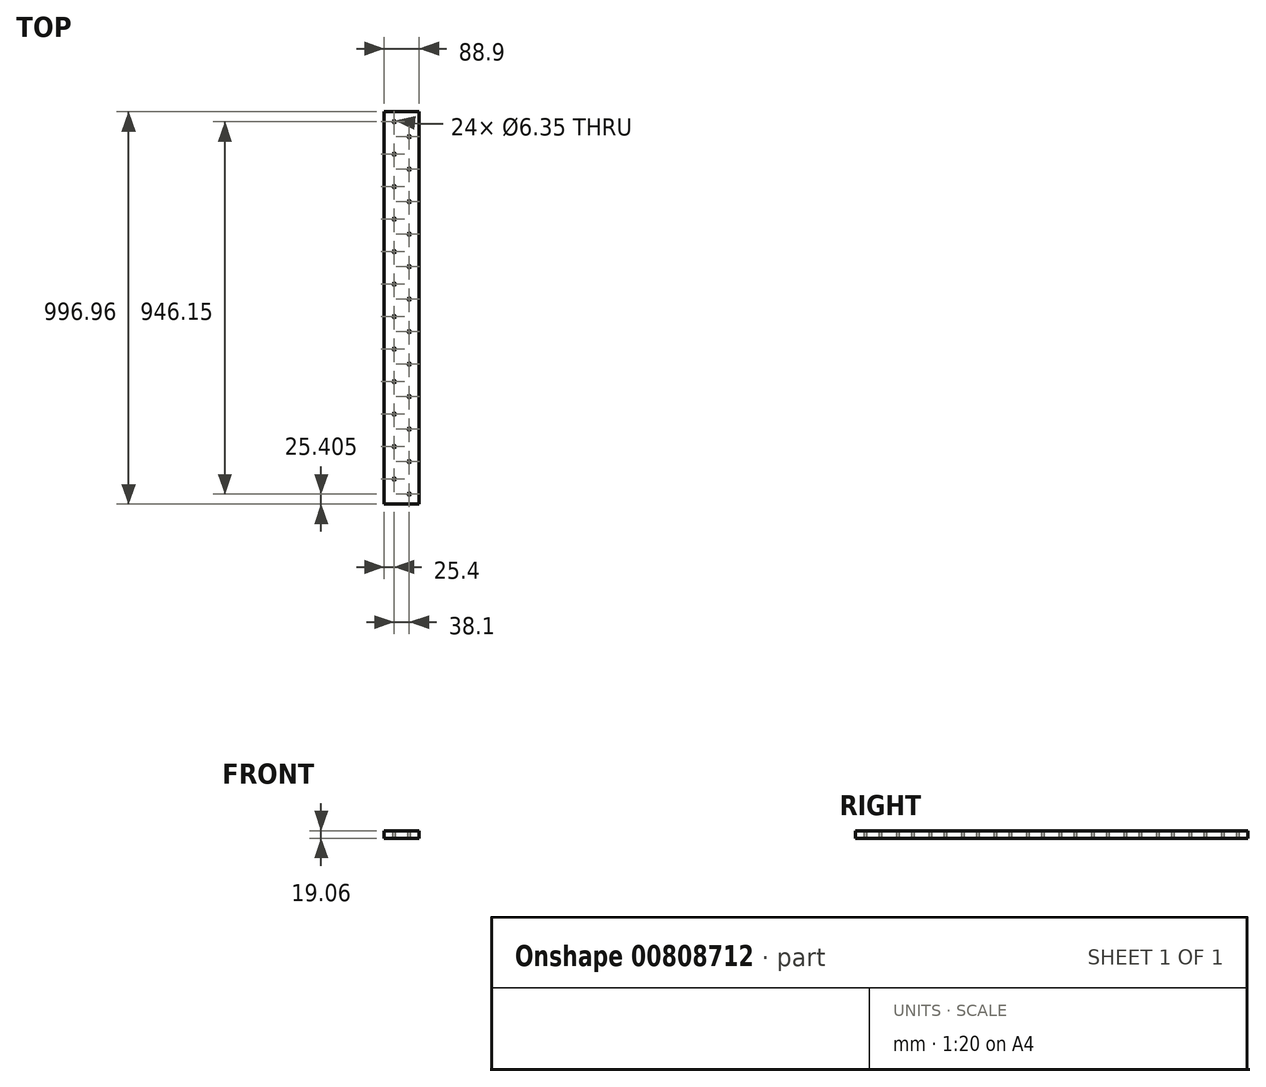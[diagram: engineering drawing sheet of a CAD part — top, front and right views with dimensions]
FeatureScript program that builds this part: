
annotation { "Feature Type Name" : "Feature", "Feature Type Description" : "" }
export const myFeature = defineFeature(function(context is Context, id is Id, definition is map)
    precondition{}
    {
        {
            var Q0;
            Q0=qCreatedBy(makeId("Front.planeOp"),FACE);
            var sketch = newSketch(context, id + "F0", { "sketchPlane" : qUnion([Q0])});
            skLineSegment(sketch, "E0.bottom", {"start": v(-44.45, 9.52) * mm, "end": v(44.45, 9.52) * mm});
            skLineSegment(sketch, "E0.top", {"start": v(-44.45, -9.53) * mm, "end": v(44.45, -9.53) * mm});
            skLineSegment(sketch, "E0.left", {"start": v(-44.45, 9.52) * mm, "end": v(-44.45, -9.53) * mm});
            skLineSegment(sketch, "E0.right", {"start": v(44.45, 9.52) * mm, "end": v(44.45, -9.53) * mm});
            skLineSegment(sketch, "E1", {"start": v(-44.45, -9.53) * mm, "end": v(44.45, 9.52) * mm, "construction": true});
            skSolve(sketch);
        }
        {
            var Q0;
            Q0=makeQuery(id+"F0.imprint","IMPRINT",FACE,{"disambiguationData":[TD([[makeQuery(id+"F0.imprint","IMPRINT",EDGE,{"derivedFrom":sQuery(id+"F0.wireOp",EDGE,"E0.bottom")}),-1.0]])]});
            extrude(context, id + "F1", {"entities" : qUnion([Q0]), "flatOperationType" : FlatOperationType.REMOVE, "depth" : 996.95 * mm, "offsetDistance" : 25.4 * mm, "domain" : OperationDomain.MODEL, "symmetric" : true});
        }
        {
            var Q0;
            Q0=makeQuery(id+"F1.opExtrude","SWEPT_FACE",FACE,{"disambiguationData":[OSD([sQuery(id+"F0.wireOp",EDGE,"E0.bottom")])]});
            var sketch = newSketch(context, id + "F2", { "sketchPlane" : qUnion([Q0])});
            skLineSegment(sketch, "E2.bottom", {"start": v(-19.05, -434.98) * mm, "end": v(19.05, -434.98) * mm, "construction": true});
            skLineSegment(sketch, "E2.left", {"start": v(-19.05, -434.98) * mm, "end": v(-19.05, -473.08) * mm, "construction": true});
            skLineSegment(sketch, "E2.right", {"start": v(19.05, -434.98) * mm, "end": v(19.05, -473.08) * mm, "construction": true});
            skLineSegment(sketch, "E3", {"start": v(-19.05, -473.08) * mm, "end": v(19.05, -473.08) * mm, "construction": true});
            skLineSegment(sketch, "E4", {"start": v(0, -473.08) * mm, "end": v(0, -498.48) * mm, "construction": true});
            skCircle(sketch, "E5", {"center": v(19.05, -473.08) * mm, "radius": 3.18 * mm});
            skCircle(sketch, "E6", {"center": v(-19.05, -434.98) * mm, "radius": 3.18 * mm});
            skCircle(sketch, "E7.0.1.0", {"center": v(-19.05, -352.43) * mm, "radius": 3.18 * mm});
            skCircle(sketch, "E7.0.1.1", {"center": v(19.05, -390.53) * mm, "radius": 3.18 * mm});
            skCircle(sketch, "E7.0.2.0", {"center": v(-19.05, -269.88) * mm, "radius": 3.18 * mm});
            skCircle(sketch, "E7.0.2.1", {"center": v(19.05, -307.98) * mm, "radius": 3.18 * mm});
            skCircle(sketch, "E7.0.3.0", {"center": v(-19.05, -187.33) * mm, "radius": 3.18 * mm});
            skCircle(sketch, "E7.0.3.1", {"center": v(19.05, -225.43) * mm, "radius": 3.18 * mm});
            skCircle(sketch, "E7.0.4.0", {"center": v(-19.05, -104.78) * mm, "radius": 3.18 * mm});
            skCircle(sketch, "E7.0.4.1", {"center": v(19.05, -142.88) * mm, "radius": 3.18 * mm});
            skCircle(sketch, "E7.0.5.0", {"center": v(-19.05, -22.23) * mm, "radius": 3.18 * mm});
            skCircle(sketch, "E7.0.5.1", {"center": v(19.05, -60.33) * mm, "radius": 3.18 * mm});
            skCircle(sketch, "E7.0.6.0", {"center": v(-19.05, 60.32) * mm, "radius": 3.18 * mm});
            skCircle(sketch, "E7.0.6.1", {"center": v(19.05, 22.22) * mm, "radius": 3.18 * mm});
            skCircle(sketch, "E7.0.7.0", {"center": v(-19.05, 142.87) * mm, "radius": 3.18 * mm});
            skCircle(sketch, "E7.0.7.1", {"center": v(19.05, 104.77) * mm, "radius": 3.18 * mm});
            skCircle(sketch, "E7.0.8.0", {"center": v(-19.05, 225.42) * mm, "radius": 3.18 * mm});
            skCircle(sketch, "E7.0.8.1", {"center": v(19.05, 187.32) * mm, "radius": 3.18 * mm});
            skCircle(sketch, "E7.0.9.0", {"center": v(-19.05, 307.97) * mm, "radius": 3.18 * mm});
            skCircle(sketch, "E7.0.9.1", {"center": v(19.05, 269.87) * mm, "radius": 3.18 * mm});
            skCircle(sketch, "E7.0.10.0", {"center": v(-19.05, 390.52) * mm, "radius": 3.18 * mm});
            skCircle(sketch, "E7.0.10.1", {"center": v(19.05, 352.42) * mm, "radius": 3.18 * mm});
            skLineSegment(sketch, "E7.direction1", {"start": v(-19.05, -434.98) * mm, "end": v(8.37, -434.98) * mm, "construction": true});
            skLineSegment(sketch, "E7.direction2", {"start": v(-19.05, -434.98) * mm, "end": v(-19.05, -352.43) * mm, "construction": true});
            skCircle(sketch, "E8.0.0.11", {"center": v(-19.05, 473.07) * mm, "radius": 3.18 * mm});
            skCircle(sketch, "E8.2.0.11", {"center": v(19.05, 434.97) * mm, "radius": 3.18 * mm});
            skSolve(sketch);
        }
        {
            var Q0;
            Q0 = qSketchRegion(id + "F2", true);
            extrude(context, id + "F3", {"entities" : qUnion([Q0]), "operationType" : NewBodyOperationType.REMOVE, "endBound" : BoundingType.UP_TO_NEXT, "oppositeDirection" : true, "depth" : 25.4 * mm, "offsetDistance" : 25.4 * mm});
        }
    });
